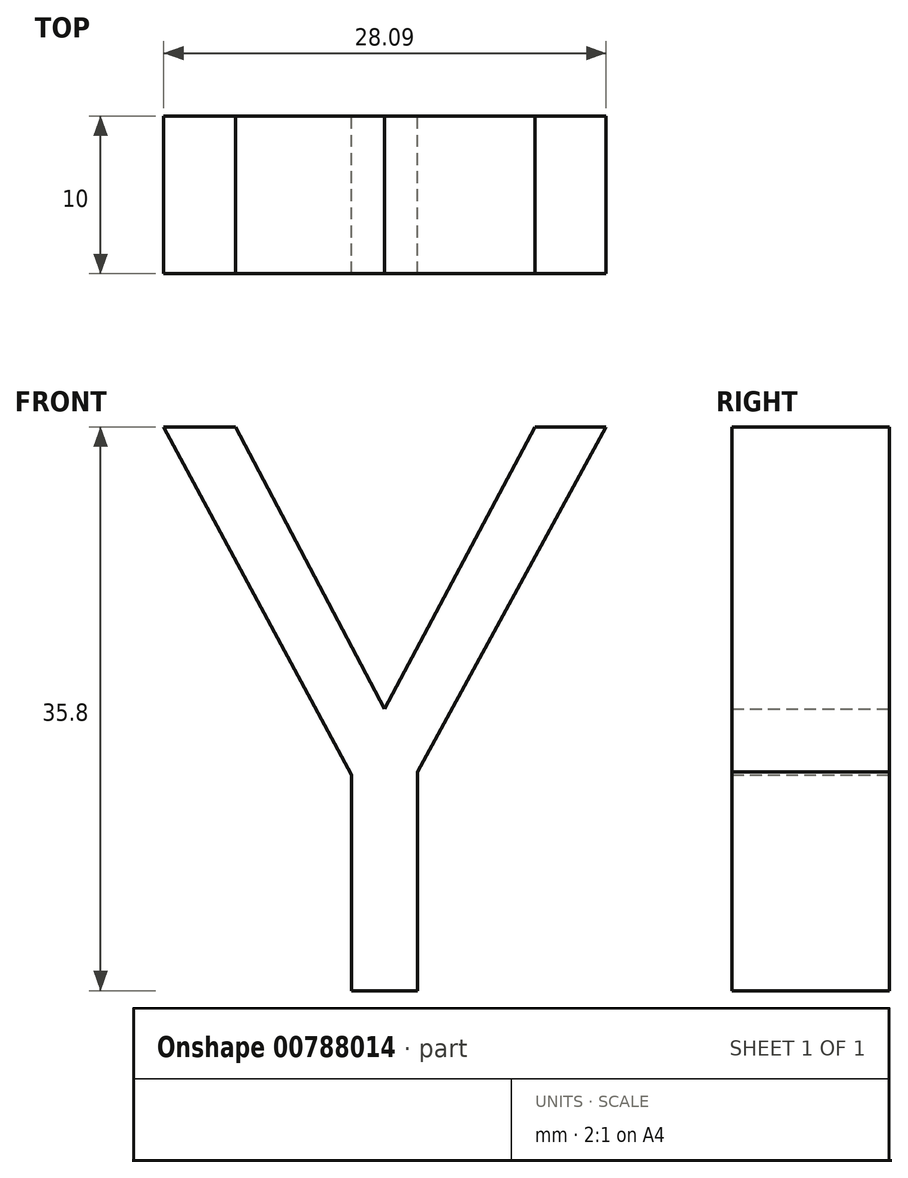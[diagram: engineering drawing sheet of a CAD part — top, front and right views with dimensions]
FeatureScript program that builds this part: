
annotation { "Feature Type Name" : "Feature", "Feature Type Description" : "" }
export const myFeature = defineFeature(function(context is Context, id is Id, definition is map)
    precondition{}
    {
        {
            var Q0;
            Q0=qCreatedBy(makeId("Front.planeOp"),FACE);
            var sketch = newSketch(context, id + "F0", { "sketchPlane" : qUnion([Q0])});
            skText(sketch, "E0", { "text": "Y", "fontName": "OpenSans-Regular.ttf"});
            const initialGuessF0  = {"E0": [-0.03134, 0, 1, 0, 0.03611]};
            skSetInitialGuess(sketch, initialGuessF0);
            skSolve(sketch);
        }
        {
            var Q0;
            Q0 = qSketchRegion(id + "F0", true);
            extrude(context, id + "F1", {"entities" : qUnion([Q0]), "depth" : 10 * mm, "offsetDistance" : 25.4 * mm});
        }
    });
